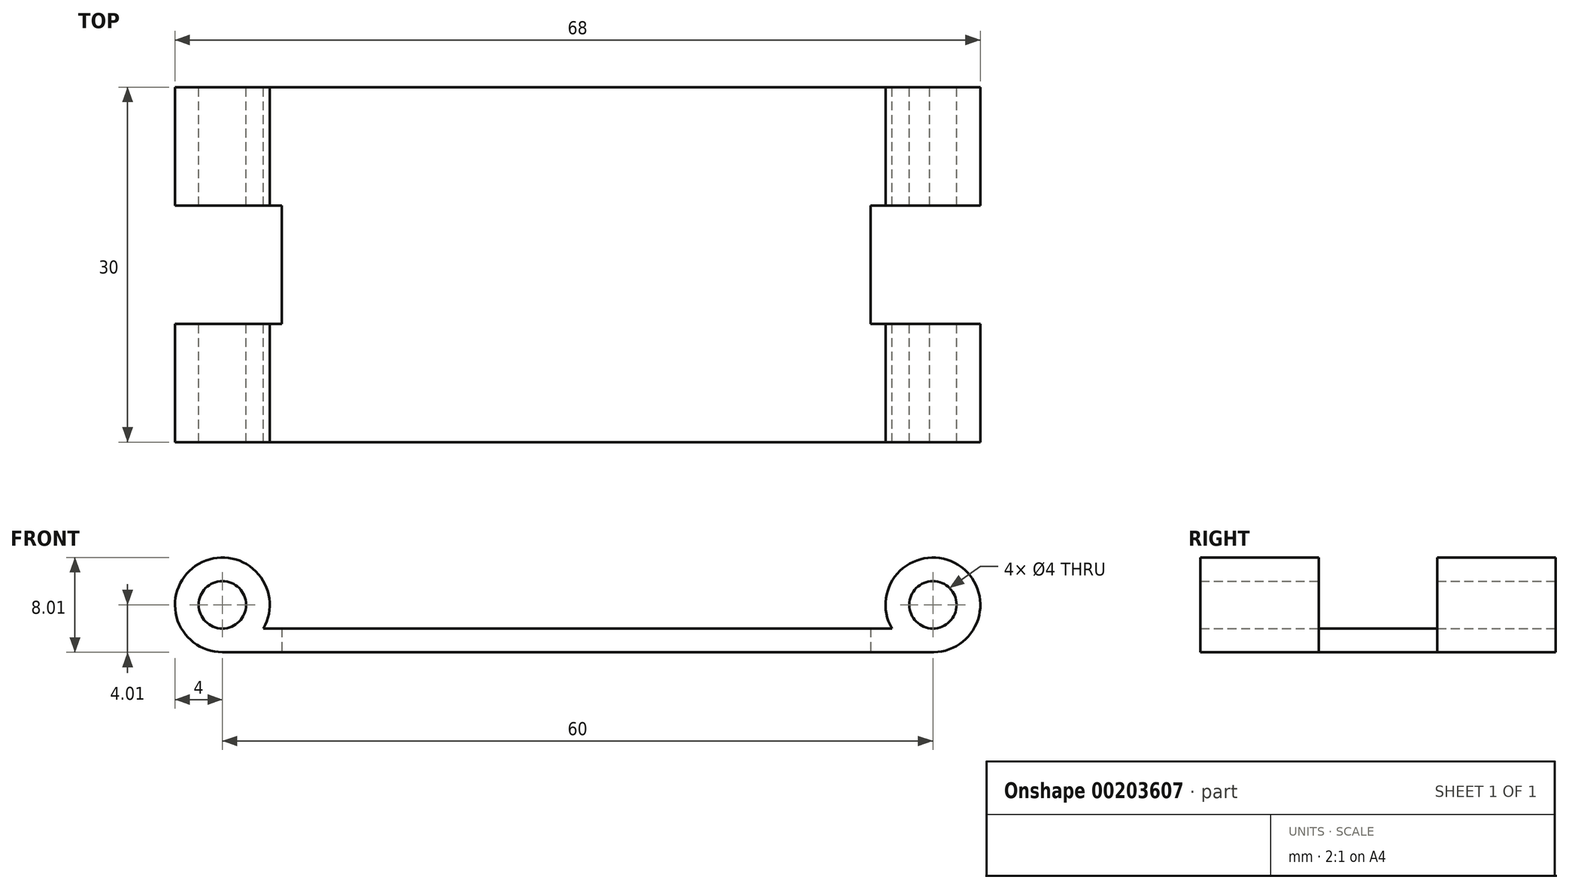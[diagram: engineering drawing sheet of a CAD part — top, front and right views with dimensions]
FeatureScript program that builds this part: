
annotation { "Feature Type Name" : "Feature", "Feature Type Description" : "" }
export const myFeature = defineFeature(function(context is Context, id is Id, definition is map)
    precondition{}
    {
        {
            var Q0;
            Q0=qCreatedBy(makeId("Front.planeOp"),FACE);
            var sketch = newSketch(context, id + "F0", { "sketchPlane" : qUnion([Q0])});
            skCircle(sketch, "E0", {"center": v(0, 0) * mm, "radius": 4 * mm});
            skCircle(sketch, "E1", {"center": v(0, 0) * mm, "radius": 1.5 * mm});
            skLineSegment(sketch, "E2.bottom", {"start": v(0, -4) * mm, "end": v(60, -4) * mm});
            skLineSegment(sketch, "E2.top", {"start": v(0, -2) * mm, "end": v(60, -2) * mm});
            skLineSegment(sketch, "E2.left", {"start": v(0, -4) * mm, "end": v(0, -2) * mm});
            skLineSegment(sketch, "E2.right", {"start": v(60, -4) * mm, "end": v(60, -2) * mm});
            skLineSegment(sketch, "E3", {"start": v(60, -2) * mm, "end": v(60, 0) * mm});
            skCircle(sketch, "E4", {"center": v(60, 0) * mm, "radius": 4 * mm});
            skCircle(sketch, "E5", {"center": v(60, 0) * mm, "radius": 1.5 * mm});
            skCircle(sketch, "E6", {"center": v(60, 0) * mm, "radius": 2 * mm});
            skCircle(sketch, "E7", {"center": v(0, 0) * mm, "radius": 2 * mm});
            skSolve(sketch);
        }
        {
            var Q0;
            {var subQ0=sQuery(id+"F0.wireOp",EDGE,"E2.left");Q0=makeQuery(id+"F0.imprint","IMPRINT",FACE,{"disambiguationData":[TD([[makeQuery(id+"F0.imprint","IMPRINT",EDGE,{"derivedFrom":subQ0}),-1.0]])]});}
            var Q1;
            {var subQ1=sQuery(id+"F0.wireOp",EDGE,"E0");var subQ3=sQuery(id+"F0.wireOp",EDGE,"E2.top");var subQ4=makeQuery(id+"F0.imprint","INTERSECT",VERTEX,{"derivedFrom":[subQ1,subQ3]});Q1=makeQuery(id+"F0.imprint","IMPRINT",FACE,{"disambiguationData":[TD([[makeQuery(id+"F0.imprint","IMPRINT",EDGE,{"disambiguationData":[TD([[subQ4,-1.0]])],"derivedFrom":subQ3}),-1.0]])]});}
            var Q2;
            {var subQ0=sQuery(id+"F0.wireOp",EDGE,"E2.right");Q2=makeQuery(id+"F0.imprint","IMPRINT",FACE,{"disambiguationData":[TD([[makeQuery(id+"F0.imprint","IMPRINT",EDGE,{"derivedFrom":subQ0}),1.0]])]});}
            var Q3;
            {var subQ1=sQuery(id+"F0.wireOp",EDGE,"E2.bottom");var subQ5=sQuery(id+"F0.wireOp",EDGE,"E2.right");var subQ6=makeQuery(id+"F0.imprint","INTERSECT",VERTEX,{"derivedFrom":[subQ1,subQ5]});Q3=makeQuery(id+"F0.imprint","IMPRINT",FACE,{"disambiguationData":[TD([[makeQuery(id+"F0.imprint","IMPRINT",EDGE,{"disambiguationData":[TD([[subQ6,1.0]])],"derivedFrom":subQ1}),-1.0]])]});}
            var Q4;
            {var subQ0=sQuery(id+"F0.wireOp",EDGE,"E2.left");Q4=makeQuery(id+"F0.imprint","IMPRINT",FACE,{"disambiguationData":[TD([[makeQuery(id+"F0.imprint","IMPRINT",EDGE,{"derivedFrom":subQ0}),1.0]])]});}
            extrude(context, id + "F1", {"entities" : qUnion([Q0, Q1, Q2, Q3, Q4]), "depth" : 30 * mm});
        }
        {
            var Q0;
            Q0=makeQuery(id+"F1.opExtrude","SWEPT_FACE",FACE,{"disambiguationData":[OSD([sQuery(id+"F0.wireOp",EDGE,"E2.bottom")])]});
            var sketch = newSketch(context, id + "F2", { "sketchPlane" : qUnion([Q0])});
            skPoint(sketch, "E8", {"position": v(59.74, 10) * mm});
            skPoint(sketch, "E9", {"position": v(59.74, 20) * mm});
            skLineSegment(sketch, "E10", {"start": v(59.74, 10) * mm, "end": v(54.74, 10) * mm});
            skLineSegment(sketch, "E11", {"start": v(54.74, 10) * mm, "end": v(54.74, 20) * mm});
            skLineSegment(sketch, "E12", {"start": v(54.74, 20) * mm, "end": v(64.74, 20) * mm});
            skLineSegment(sketch, "E13", {"start": v(64.74, 20) * mm, "end": v(64.74, 10) * mm});
            skLineSegment(sketch, "E14", {"start": v(64.74, 10) * mm, "end": v(59.74, 10) * mm});
            skPoint(sketch, "E15", {"position": v(0, 10) * mm});
            skPoint(sketch, "E16", {"position": v(4.94, 20) * mm});
            skLineSegment(sketch, "E17", {"start": v(0, 10) * mm, "end": v(-4, 10) * mm});
            skLineSegment(sketch, "E18", {"start": v(-4, 10) * mm, "end": v(-4, 20) * mm});
            skLineSegment(sketch, "E19", {"start": v(-4, 20) * mm, "end": v(5, 20) * mm});
            skLineSegment(sketch, "E20", {"start": v(5, 20) * mm, "end": v(5, 10) * mm});
            skLineSegment(sketch, "E21", {"start": v(5, 10) * mm, "end": v(0, 10) * mm});
            skLineSegment(sketch, "E22", {"start": v(0, 10) * mm, "end": v(0, 0) * mm});
            skSolve(sketch);
        }
        {
            var Q0;
            {var subQ0=sQuery(id+"F2.wireOp",EDGE,"E10");Q0=makeQuery(id+"F2.imprint","IMPRINT",FACE,{"disambiguationData":[TD([[makeQuery(id+"F2.imprint","IMPRINT",EDGE,{"derivedFrom":subQ0}),-1.0]])]});}
            var Q1;
            {var subQ0=sQuery(id+"F2.wireOp",EDGE,"E13");Q1=makeQuery(id+"F2.imprint","IMPRINT",FACE,{"disambiguationData":[TD([[makeQuery(id+"F2.imprint","IMPRINT",EDGE,{"derivedFrom":subQ0}),-1.0]])]});}
            extrude(context, id + "F3", {"entities" : qUnion([Q0, Q1]), "operationType" : NewBodyOperationType.REMOVE, "endBound" : BoundingType.SYMMETRIC, "oppositeDirection" : true, "depth" : 50 * mm});
        }
        {
            var Q0;
            {var subQ0=sQuery(id+"F2.wireOp",EDGE,"E17");Q0=makeQuery(id+"F2.imprint","IMPRINT",FACE,{"disambiguationData":[TD([[makeQuery(id+"F2.imprint","IMPRINT",EDGE,{"derivedFrom":subQ0}),-1.0]])]});}
            var Q1;
            {var subQ0=sQuery(id+"F2.wireOp",EDGE,"E20");Q1=makeQuery(id+"F2.imprint","IMPRINT",FACE,{"disambiguationData":[TD([[makeQuery(id+"F2.imprint","IMPRINT",EDGE,{"derivedFrom":subQ0}),-1.0]])]});}
            extrude(context, id + "F4", {"entities" : qUnion([Q0, Q1]), "operationType" : NewBodyOperationType.REMOVE, "endBound" : BoundingType.SYMMETRIC, "oppositeDirection" : true, "depth" : 50 * mm});
        }
    });
